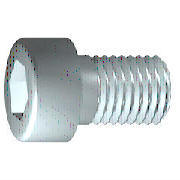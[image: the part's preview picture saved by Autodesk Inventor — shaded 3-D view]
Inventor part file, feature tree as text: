
AUTODESK INVENTOR PART (.ipt)
format: ipt  version: 2013 (Build 170138000, 138)  size: 182,784 bytes
history: native  units: mm (DEFAULTED — no unit token found)
features: sketch x2, extrude x1, plane x1
ambient origin geometry x7: Origin, YZ Plane, XY Plane, X Axis, Y Axis, Z Axis, Center Point
bodies: Solid1 (feature_tree), Body (feature_tree)
feature tree (4):
  extrude  "Slot"  Depth=3.1751mm
  plane  "Work Plane1"
  sketch  "Sketch1"  dims[d1=31.75mm d2=3.1751mm]
  sketch  "Sketch2"  dims[d3=6.35mm d4=3.048mm d5=60.0deg d6=6.35mm d7=6.35mm d8=5.513926mm d9=9.525mm d10=90.0deg d11=10.0mm d12=0.0mm d13=31.75mm d14=0.0mm d15=0.75565mm d16=0.75565mm d17=0.635mm d19=0.0mm d26=44.45mm d27=45.0deg d28=0.0mm d29=0.0mm]
